# Revit family: Platek_Tarsius_Pole with 1 Luminair
name_source: partatom
category: Apparecchi per illuminazione
revit_build: Autodesk Revit 2017 (Build: 20160225_1515(x64)
units: mm (PartAtom-declared; Revit-internal decimal feet)

## family parameters
Basato su piano di lavoro = Sì
Condiviso = Sì
Punto di calcolo locali = No
Quota connettore circolare = Usa diametro
Sempre verticale = No
Sorgente d'illuminazione = Sì
Taglio con vuoti quando caricato = No
Tipo di parte = Normale

## types (12) — shared parameters
Angolo inclinazione = 90.00°
Beam Angle = 0.00°
Body = PLK_Grey
CRI = >80
Cable Lenght = Cable length 8 m
Carico apparente = 0 VA
Colour Temperature = 3000 K
Commenti sul tipo = Parking areas, Urban zones, Roads
Descrizione = Outdoor Lighting, Street and Park areas
Diffuse Type = 4mm PMMA transparent difuser
Energy Efficiency Rating = A/A+/A++
Filtro dei colori = 16777215
Frequency = 0/50/60 Hz
IK Rating = IK 10
IP Rating = IP66
Immagine tipo = tarsius_pole.jpg
Insulation Class = 2
LED Protection = Surge protection included
Lampada = LED
Light Source = PLK_Light Source
Modello = Tarsius
Mounting Type = Ground
Nota chiave = Other Led colors available on request
PLATEK FInishes = Painted Aluminium Avalaible in Anthracite/Black/White/Corten/Bronze
Power Supply Unit = Included
Product Dimension = L498mm x W350mm x H60mm
Product Documentation Link = http://www.platek.eu
Product Page URL = http://www.platek.eu
Produttore = PLATEK SRL
Prospetto di default = 1219.2 mm  [stored 4 ft]
Rendi la forma visibile nel rendering = No
Supply Voltage = 230 V
Supply Voltage Max = 240 V
Supply Voltage Min = 220 V
URL = www.platek.eu
Variazione temperatura colore lampada con luminosità attenuata = <Nessuno>

## per-type parameters (varying)
| type | Aluminium | Codice assieme | Dimmable | Emetti da larghezza rettangolo | Emetti da lunghezza rettangolo | File diagramma fotometrico | H Pole 2730 | H Pole 930 | H Pole3000 | H Pole5000 | H Pole5200 | Heght Pole 1 | Heght Pole 2 | Luminaire Luminous Flux | Luminaire Luminous Intensity | Luminaire Wattage | Manufacturer Comment | PLATEK Article Code | Pole Dimension |
| 8750918_57,8W_LED_3000K_H4000mm | PLK_Light Source | 8750918.06(Grey); 8750918.08(Anthracite); 8750918.01(Black); 8750918.02(White); 8750918.07(Corten); 8750918.09(Bronze) | DALI | 260 mm  [stored 0.853018 ft] | 196 mm  [stored 0.643045 ft] | 8750918.IES | No | Sì | Sì | No | No | 3000 mm  [stored 9.84252 ft] | 930 mm  [stored 3.05118 ft] | 5116 lm | 2942 cd | 58 W | Transparent Diffuser and Street Optic | 8750918 | Ø88,9mm H4000mm |
| 8750719_50,5W_LED_3000K_H4000mm | PLK_Light Source | 8750719.06(Grey); 8750719.08(Anthracite); 8750719.01(Black); 8750719.02(White); 8750719.07(Corten); 8750719.09(Bronze) | Midnight | 260 mm  [stored 0.853018 ft] | 196 mm  [stored 0.643045 ft] | 8750719.IES | No | Sì | Sì | No | No | 3000 mm  [stored 9.84252 ft] | 930 mm  [stored 3.05118 ft] | 4245 lm | 2441 cd | 51 W | Transparent Diffuser and Asymmetrical Optic | 8750719 | Ø88,9mm H4000mm |
| 8750718_50,5W_LED_3000K_H4000mm | PLK_Aluminium | 8750718.06(Grey); 8750718.08(Anthracite); 8750718.01(Black); 8750718.02(White); 8750718.07(Corten); 8750718.09(Bronze) | Midnight | 260 mm  [stored 0.853018 ft] | 196 mm  [stored 0.643045 ft] | 8750718.IES | No | Sì | Sì | No | No | 3000 mm  [stored 9.84252 ft] | 930 mm  [stored 3.05118 ft] | 4245 lm | 2441 cd | 51 W | Transparent Diffuser and Street Optic | 8750718 | Ø88,9mm H4000mm |
| 8750919_57,8W_LED_3000K_H4000mm | PLK_Light Source | 8750919.06(Grey); 8750919.08(Anthracite); 8750919.01(Black); 8750919.02(White); 8750919.07(Corten); 8750919.09(Bronze) | DALI | 260 mm  [stored 0.853018 ft] | 196 mm  [stored 0.643045 ft] | 8750919.IES | No | Sì | Sì | No | No | 3000 mm  [stored 9.84252 ft] | 930 mm  [stored 3.05118 ft] | 4584 lm | 2702 cd | 58 W | Transparent Diffuser and Asymmetrical Optic | 8750919 | Ø88,9mm H6000mm |
| 8750718_50,5W_LED_3000K_H6000mm | PLK_Aluminium | 8750718.06(Grey); 8750718.08(Anthracite); 8750718.01(Black); 8750718.02(White); 8750718.07(Corten); 8750718.09(Bronze) | Midnight | 196 mm  [stored 0.643045 ft] | 260 mm  [stored 0.853018 ft] | 8750718.IES | No | Sì | No | Sì | No | 5000 mm  [stored 16.4042 ft] | 930 mm  [stored 3.05118 ft] | 4245 lm | 2441 cd | 51 W | Transparent Diffuser and Street Optic | 8750718 | Ø88,9mm H6000mm |
| 8750718_50,5W_LED_3000K_H8000mm | PLK_Aluminium | 8750718.06(Grey); 8750718.08(Anthracite); 8750718.01(Black); 8750718.02(White); 8750718.07(Corten); 8750718.09(Bronze) | Midnight | 260 mm  [stored 0.853018 ft] | 196 mm  [stored 0.643045 ft] | 8750718.IES | Sì | No | No | No | Sì | 5200 mm  [stored 17.0604 ft] | 2730 mm  [stored 8.95669 ft] | 4245 lm | 2441 cd | 51 W | Transparent Diffuser and Street Optic | 8750718 | Ø88,9mm H8000mm |
| 8750719_50,7W_LED_3000K_H6000mm | PLK_Light Source | 8750719.06(Grey); 8750719.08(Anthracite); 8750719.01(Black); 8750719.02(White); 8750719.07(Corten); 8750719.09(Bronze) | Midnight | 260 mm  [stored 0.853018 ft] | 196 mm  [stored 0.643045 ft] | 8750719.IES | No | Sì | No | Sì | No | 5000 mm  [stored 16.4042 ft] | 930 mm  [stored 3.05118 ft] | 4245 lm | 2441 cd | 51 W | Transparent Diffuser and Asymmetrical Optic | 8750719 | Ø88,9mm H6000mm |
| 8750719_50,7W_LED_3000K_H8000mm | PLK_Light Source | 8750719.06(Grey); 8750719.08(Anthracite); 8750719.01(Black); 8750719.02(White); 8750719.07(Corten); 8750719.09(Bronze) | Midnight | 260 mm  [stored 0.853018 ft] | 196 mm  [stored 0.643045 ft] | 8750719.IES | Sì | No | No | No | Sì | 5200 mm  [stored 17.0604 ft] | 2730 mm  [stored 8.95669 ft] | 4245 lm | 2441 cd | 51 W | Transparent Diffuser and Asymmetrical Optic | 8750719 | Ø88,9mm H8000mm |
| 8750918_57,8W_LED_3000K_H6000mm | PLK_Light Source | 8750918.06(Grey); 8750918.08(Anthracite); 8750918.01(Black); 8750918.02(White); 8750918.07(Corten); 8750918.09(Bronze) | DALI | 260 mm  [stored 0.853018 ft] | 196 mm  [stored 0.643045 ft] | 8750918.IES | No | Sì | No | Sì | No | 5000 mm  [stored 16.4042 ft] | 930 mm  [stored 3.05118 ft] | 5116 lm | 2942 cd | 58 W | Transparent Diffuser and Street Optic | 8750918 | Ø88,9mm H6000mm |
| 8750918_57,8W_LED_3000K_H8000mm | PLK_Light Source | 8750918.06(Grey); 8750918.08(Anthracite); 8750918.01(Black); 8750918.02(White); 8750918.07(Corten); 8750918.09(Bronze) | DALI | 260 mm  [stored 0.853018 ft] | 196 mm  [stored 0.643045 ft] | 8750918.IES | Sì | No | No | No | Sì | 5200 mm  [stored 17.0604 ft] | 2730 mm  [stored 8.95669 ft] | 5116 lm | 2942 cd | 58 W | Transparent Diffuser and Street Optic | 8750918 | Ø88,9mm H6000mm |
| 8750919_57,8W_LED_3000K_H6000mm | PLK_Light Source | 8750919.06(Grey); 8750919.08(Anthracite); 8750919.01(Black); 8750919.02(White); 8750919.07(Corten); 8750919.09(Bronze) | DALI | 260 mm  [stored 0.853018 ft] | 196 mm  [stored 0.643045 ft] | 8750919.IES | No | Sì | No | Sì | No | 5000 mm  [stored 16.4042 ft] | 930 mm  [stored 3.05118 ft] | 4584 lm | 2702 cd | 58 W | Transparent Diffuser and Asymmetrical Optic | 8750919 | Ø88,9mm H6000mm |
| 8750919_57,8W_LED_3000K_H8000mm | PLK_Light Source | 8750919.06(Grey); 8750919.08(Anthracite); 8750919.01(Black); 8750919.02(White); 8750919.07(Corten); 8750919.09(Bronze) | DALI | 260 mm  [stored 0.853018 ft] | 196 mm  [stored 0.643045 ft] | 8750918.IES | Sì | No | No | No | Sì | 5200 mm  [stored 17.0604 ft] | 2730 mm  [stored 8.95669 ft] | 4584 lm | 2702 cd | 58 W | Transparent Diffuser and Asymmetrical Optic | 8750919 | Ø88,9mm H8000mm |

note: [stored X ft] marks values corroborated as IEEE doubles in the binary element streams (Revit-internal decimal feet)
